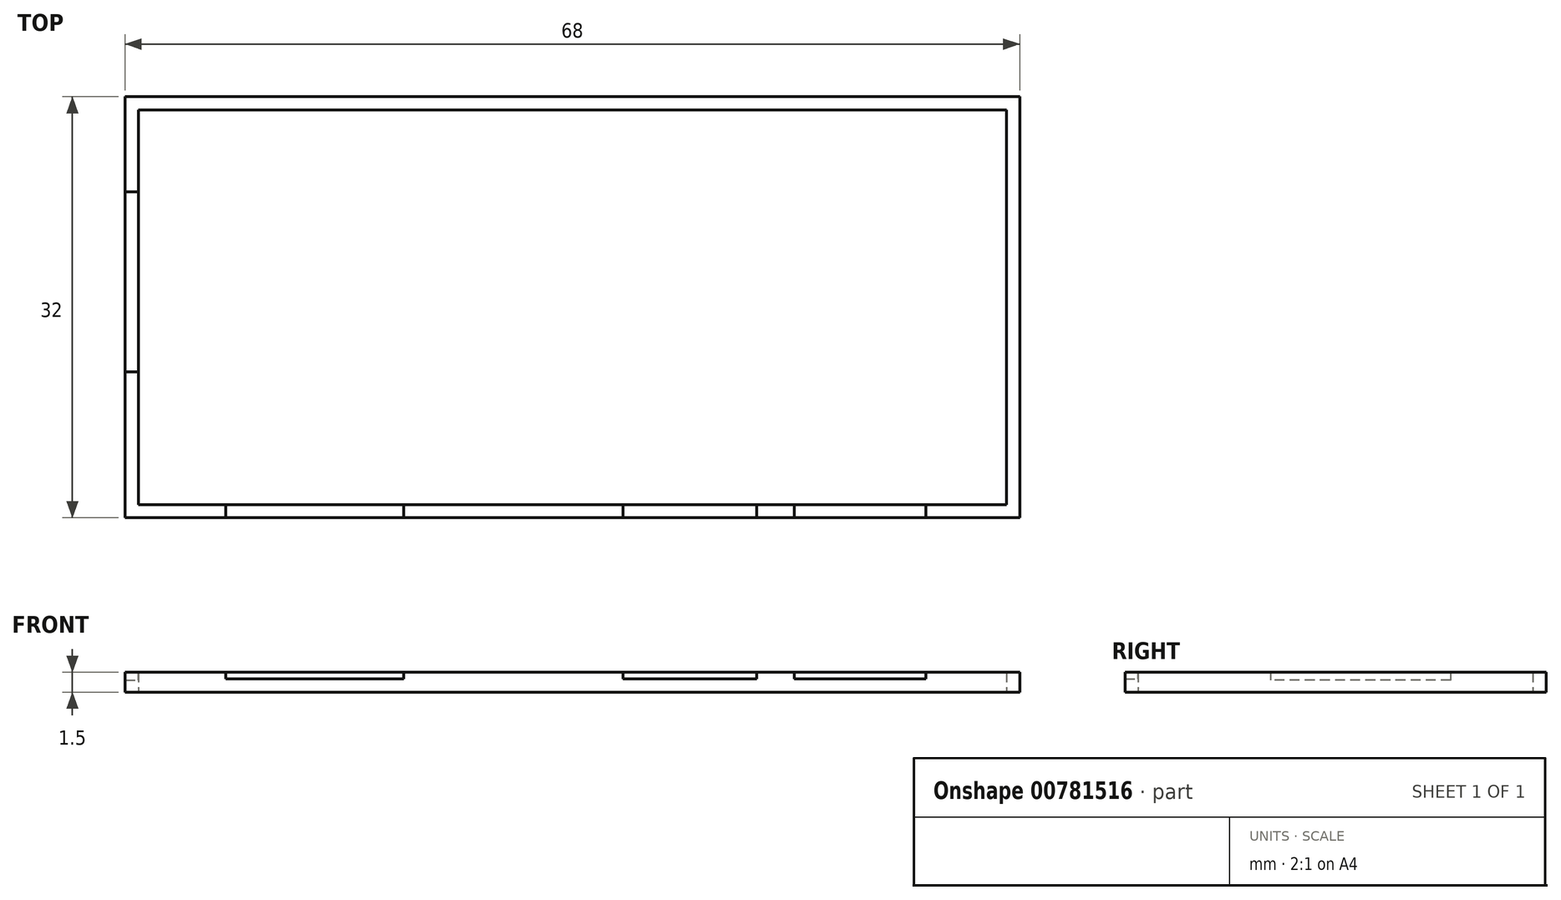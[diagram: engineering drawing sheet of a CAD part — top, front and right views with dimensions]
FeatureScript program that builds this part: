
annotation { "Feature Type Name" : "Feature", "Feature Type Description" : "" }
export const myFeature = defineFeature(function(context is Context, id is Id, definition is map)
    precondition{}
    {
        {
            var Q0;
            Q0=qCreatedBy(makeId("Top.planeOp"),FACE);
            var sketch = newSketch(context, id + "F0", { "sketchPlane" : qUnion([Q0])});
            skLineSegment(sketch, "E0.bottom", {"start": v(-34, 15.91) * mm, "end": v(34, 15.91) * mm});
            skLineSegment(sketch, "E0.top", {"start": v(-34, -16.09) * mm, "end": v(34, -16.09) * mm});
            skLineSegment(sketch, "E0.left", {"start": v(-34, 15.91) * mm, "end": v(-34, -16.09) * mm});
            skLineSegment(sketch, "E0.right", {"start": v(34, 15.91) * mm, "end": v(34, -16.09) * mm});
            skLineSegment(sketch, "E1.bottom", {"start": v(-33, 14.91) * mm, "end": v(33, 14.91) * mm});
            skLineSegment(sketch, "E1.top", {"start": v(-33, -15.09) * mm, "end": v(33, -15.09) * mm});
            skLineSegment(sketch, "E1.left", {"start": v(-33, 14.91) * mm, "end": v(-33, -15.09) * mm});
            skLineSegment(sketch, "E1.right", {"start": v(33, 14.91) * mm, "end": v(33, -15.09) * mm});
            skPoint(sketch, "E2", {"position": v(0, -15.09) * mm});
            skPoint(sketch, "E3", {"position": v(0, -16.09) * mm});
            skPoint(sketch, "E4", {"position": v(0, 14.91) * mm});
            skPoint(sketch, "E5", {"position": v(0, 15.91) * mm});
            skPoint(sketch, "E6", {"position": v(-34, -0.09) * mm});
            skPoint(sketch, "E7", {"position": v(-33, -0.09) * mm});
            skPoint(sketch, "E8", {"position": v(33, -0.09) * mm});
            skPoint(sketch, "E9", {"position": v(34, -0.09) * mm});
            skSolve(sketch);
        }
        {
            var Q0;
            Q0=qCreatedBy(makeId("Top.planeOp"),FACE);
            var sketch = newSketch(context, id + "F1", { "sketchPlane" : qUnion([Q0])});
            skLineSegment(sketch, "E10.bottom", {"start": v(-26.34, -17.54) * mm, "end": v(-12.84, -17.54) * mm});
            skLineSegment(sketch, "E10.top", {"start": v(-26.34, -9.55) * mm, "end": v(-12.84, -9.55) * mm});
            skLineSegment(sketch, "E10.left", {"start": v(-26.34, -17.54) * mm, "end": v(-26.34, -9.55) * mm});
            skLineSegment(sketch, "E10.right", {"start": v(-12.84, -17.54) * mm, "end": v(-12.84, -9.55) * mm});
            skLineSegment(sketch, "E11.bottom", {"start": v(3.84, -17.54) * mm, "end": v(14.02, -17.54) * mm});
            skLineSegment(sketch, "E11.top", {"start": v(3.84, -9.55) * mm, "end": v(14.02, -9.55) * mm});
            skLineSegment(sketch, "E11.left", {"start": v(3.84, -17.54) * mm, "end": v(3.84, -9.55) * mm});
            skLineSegment(sketch, "E11.right", {"start": v(14.02, -17.54) * mm, "end": v(14.02, -9.55) * mm});
            skLineSegment(sketch, "E12.bottom", {"start": v(16.87, -17.41) * mm, "end": v(26.88, -17.41) * mm});
            skLineSegment(sketch, "E12.top", {"start": v(16.87, -9.55) * mm, "end": v(26.88, -9.55) * mm});
            skLineSegment(sketch, "E12.left", {"start": v(16.87, -17.41) * mm, "end": v(16.87, -9.55) * mm});
            skLineSegment(sketch, "E12.right", {"start": v(26.88, -17.41) * mm, "end": v(26.88, -9.55) * mm});
            skSolve(sketch);
        }
        {
            var Q0;
            Q0=qSketchRegion(id+"F0",true);
            extrude(context, id + "F2", {"entities" : qUnion([Q0]), "depth" : 1.5 * mm, "offsetDistance" : 25 * mm});
        }
        {
            var Q0;
            Q0=qCreatedBy(makeId("Top.planeOp"),FACE);
            var sketch = newSketch(context, id + "F3", { "sketchPlane" : qUnion([Q0])});
            skLineSegment(sketch, "E13.bottom", {"start": v(-35.27, 8.67) * mm, "end": v(-25.56, 8.67) * mm});
            skLineSegment(sketch, "E13.top", {"start": v(-35.27, -5) * mm, "end": v(-25.56, -5) * mm});
            skLineSegment(sketch, "E13.left", {"start": v(-35.27, 8.67) * mm, "end": v(-35.27, -5) * mm});
            skLineSegment(sketch, "E13.right", {"start": v(-25.56, 8.67) * mm, "end": v(-25.56, -5) * mm});
            skSolve(sketch);
        }
        {
            var Q0;
            Q0=qCreatedBy(makeId("Top.planeOp"),FACE);
            var sketch = newSketch(context, id + "F4", { "sketchPlane" : qUnion([Q0])});
            skLineSegment(sketch, "E14.bottom", {"start": v(-27.35, 17.47) * mm, "end": v(27.37, 17.47) * mm});
            skLineSegment(sketch, "E14.top", {"start": v(-27.35, 9.27) * mm, "end": v(27.37, 9.27) * mm});
            skLineSegment(sketch, "E14.left", {"start": v(-27.35, 17.47) * mm, "end": v(-27.35, 9.27) * mm});
            skLineSegment(sketch, "E14.right", {"start": v(27.37, 17.47) * mm, "end": v(27.37, 9.27) * mm});
            skSolve(sketch);
        }
        {
            var Q0;
            Q0=qSketchRegion(id+"F3",true);
            extrude(context, id + "F5", {"entities" : qUnion([Q0]), "operationType" : NewBodyOperationType.REMOVE, "depth" : 3.2 * mm, "offsetDistance" : 25 * mm, "hasSecondDirection" : true, "secondDirectionOppositeDirection" : false, "secondDirectionDepth" : 0.9 * mm});
        }
        {
            var Q0;
            Q0=qSketchRegion(id+"F1",true);
            extrude(context, id + "F6", {"entities" : qUnion([Q0]), "operationType" : NewBodyOperationType.REMOVE, "depth" : 5.6 * mm, "offsetDistance" : 25 * mm, "hasSecondDirection" : true, "secondDirectionOppositeDirection" : false, "secondDirectionDepth" : 1 * mm});
        }
        {
            var Q0;
            Q0=qSketchRegion(id+"F4",true);
            extrude(context, id + "F7", {"entities" : qUnion([Q0]), "operationType" : NewBodyOperationType.REMOVE, "depth" : 5.5 * mm, "offsetDistance" : 25 * mm, "hasSecondDirection" : true, "secondDirectionOppositeDirection" : false, "secondDirectionDepth" : 1.5 * mm});
        }
    });
